# Revit family: SLVT
name_source: partatom
category: Lighting Fixtures
units: mm (PartAtom-declared; Revit-internal decimal feet)

## family parameters
Always vertical = Yes
Cut with Voids When Loaded = No
Light Source = Yes
Part Type = Normal
Room Calculation Point = No
Round Connector Dimension = Use Diameter
Shared = No
Work Plane-Based = No

## types (1)
- SLVT
    AAL IES File = SL-VT-H2-100MH.ies
    Absolute Lumens = 9300 lm
    Apparent Load = 57 VA
    Assembly Code = D5020200
    Color Filter = 16777215
    Default Elevation = 0' - 0"
    Description = Exterior Lighting
    Dimming Lamp Color Temperature Shift = <None>
    Frequency = 60 Hz
    Full Load Current = 1 A
    Glazing Type = Glass-Clear
    Height = 1' - 8"
    Housing Material = Aluminum-Matte Aluminum
    Lamp = ONE 100 METAL HALIDE ED-17 MED BASE
    Manufacturer = Architectural Area Lighting
    MasterFormat Number = 26.56.29
    MasterFormat Title = Area Lighting
    Model = SLVT
    Note Text = LF
    Note Visible = Yes
    Number of Poles = 1
    OmniClass Number = 23.80.70.14.11.14
    OmniClass Title = Post-Top Lighting
    Photometric Web File = generic.ies
    Power Factor = 1
    Reflector Material = Aluminum-Reflector
    SL Type = 0
    Series = Largent
    Tilt Angle = 60.00°
    URL = https://www.currentlighting.com
    VTH = Yes
    VTL = No
    VTLDL = No
    Voltage = 277 V
    Wattage Comments = 100W MH Ballast
    Width = 2' - 1 1/2"
    Width Radius = 1' - 0 3/4"

## geometry (parser evidence)
native form markers: Sweep x2
no freeform markers — native parametric forms only
